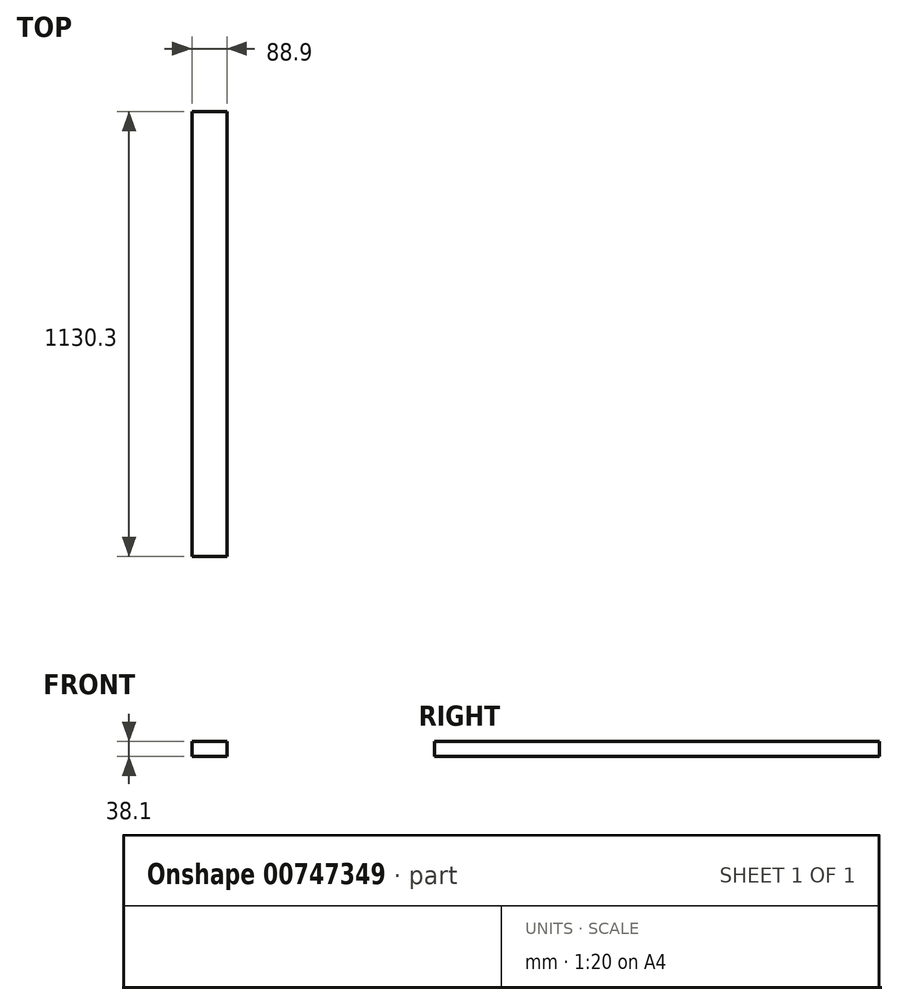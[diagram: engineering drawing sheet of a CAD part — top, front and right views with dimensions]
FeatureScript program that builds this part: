
annotation { "Feature Type Name" : "Feature", "Feature Type Description" : "" }
export const myFeature = defineFeature(function(context is Context, id is Id, definition is map)
    precondition{}
    {
        {
            var Q0;
            Q0=qCreatedBy(makeId("Front.planeOp"),FACE);
            var sketch = newSketch(context, id + "F0", { "sketchPlane" : qUnion([Q0])});
            skLineSegment(sketch, "E0.bottom", {"start": v(0, 0) * mm, "end": v(88.9, 0) * mm});
            skLineSegment(sketch, "E0.top", {"start": v(0, 38.1) * mm, "end": v(88.9, 38.1) * mm});
            skLineSegment(sketch, "E0.left", {"start": v(0, 0) * mm, "end": v(0, 38.1) * mm});
            skLineSegment(sketch, "E0.right", {"start": v(88.9, 0) * mm, "end": v(88.9, 38.1) * mm});
            skSolve(sketch);
        }
        {
            var Q0;
            Q0=qSketchRegion(id+"F0",true);
            extrude(context, id + "F1", {"entities" : qUnion([Q0]), "depth" : 1130.3 * mm, "offsetDistance" : 25.4 * mm});
        }
    });
